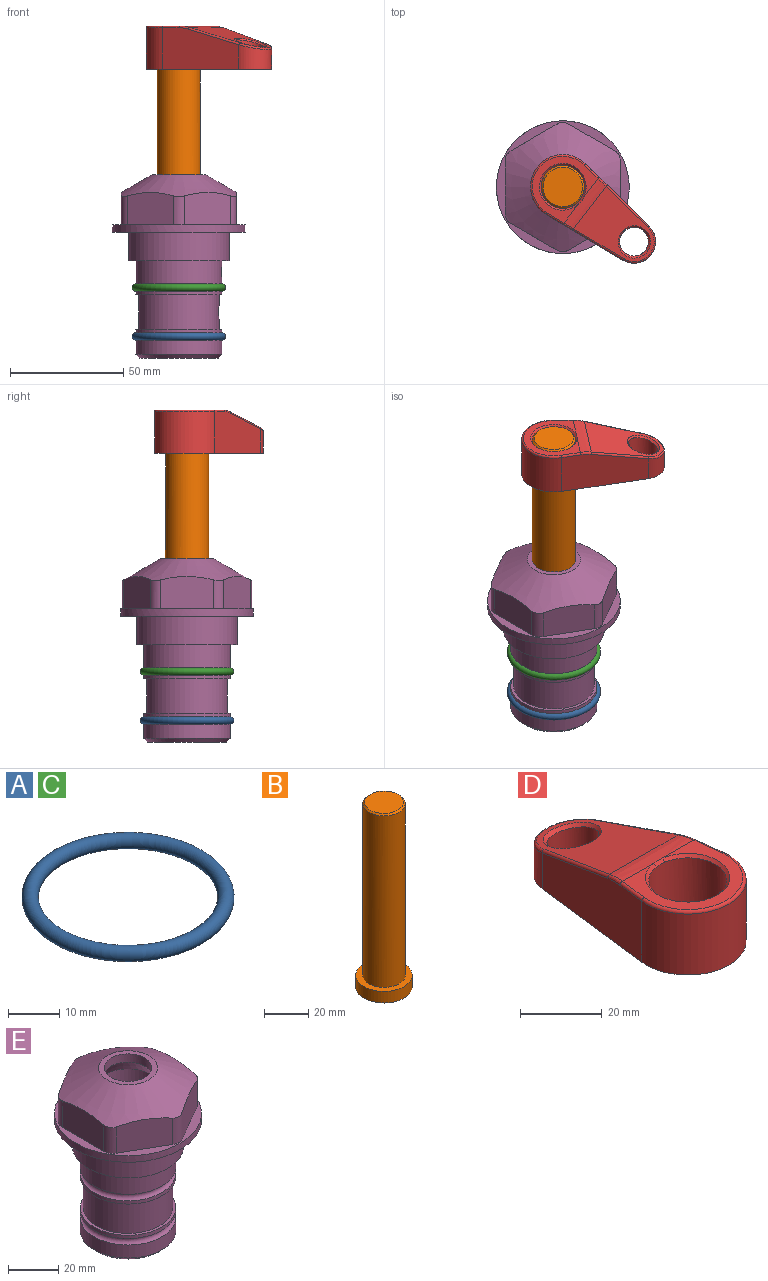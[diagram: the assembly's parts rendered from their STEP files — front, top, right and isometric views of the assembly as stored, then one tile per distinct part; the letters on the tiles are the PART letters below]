
ASSEMBLY  parts=5 mates=4
PART A: 1 faces, bbox 44.7x44.7x3.2 mm
  f0: torus R=19.05mm, axis (0,0,1), area 1193.9mm2
PART B: 6 faces, bbox 25.4x25.4x101.6 mm
  f0: plane 17.46x17.46mm, normal (0,0,1), area 239.5mm2, adj f5
  f1: plane 25.4x25.4mm, normal (0,0,-1), area 506.7mm2, adj f2
  f2: cylinder r=12.7mm len=25.4mm, axis (0,0,1), area 506.7mm2, adj f1,f3
  f3: plane 25.4x25.4mm, normal (0,0,1), area 221.7mm2, adj f2,f4
  f4: cylinder r=9.53mm len=94.46mm, axis (0,0,1), area 5653mm2, adj f3,f5
  f5: cone r=8.73mm half-angle=45deg, axis (0,0,-1), area 64.4mm2, adj f0,f4
PART C: same geometry as A
PART D: 31 faces, bbox 31.7x65.5x19.8 mm
  f0: plane 39.12x18.26mm, normal (0.99,0.12,0), area 612.2mm2, adj f1,f4,f7,f11,f13,f15
  f1: cylinder r=9.53mm len=18.91mm, axis (0,0,-1), area 296.1mm2, adj f0,f2,f7,f17
  f2: plane 39.12x18.26mm, normal (-0.99,0.12,0), area 612.2mm2, adj f1,f4,f7,f12,f14,f16
  f3: cylinder r=6.35mm len=12.7mm, axis (0,0,-1), area 362.4mm2, adj f7,f18
  f4: cylinder r=14.29mm len=28.58mm, axis (0,0,-1), area 882.2mm2, adj f0,f2,f7,f10
  f5: cylinder r=9.53mm len=19.05mm, axis (0,0,-1), area 1092.6mm2, adj f7,f19,f20
  f6: plane 26.99x23.69mm, normal (0,0,1), area 216.2mm2, adj f9,f10,f11,f12,f19
  f7: plane 63.5x28.58mm, normal (0,0,-1), area 661.8mm2, adj f0,f1,f2,f3,f4,f5,f22,f23
  f8: plane 33.52x23.6mm, normal (0,0.26,0.97), area 486mm2, adj f9,f15,f16,f17,f18
  f9: cylinder r=19.05mm len=24.72mm, axis (1,0,0), area 120.4mm2, adj f6,f8,f13,f14,f20
  f10: torus R=13.49mm, axis (0,0,1), area 59mm2, adj f4,f6,f11,f12
  f11: cylinder r=0.79mm len=8.67mm, axis (0.12,-0.99,0), area 10.8mm2, adj f0,f6,f10,f13
  f12: cylinder r=0.79mm len=8.67mm, axis (0.12,0.99,0), area 10.8mm2, adj f2,f6,f10,f14
  f13: bspline ~4.95x1.42mm, area 6.1mm2, adj f0,f9,f11,f15
  f14: bspline ~4.95x1.42mm, area 6.1mm2, adj f2,f9,f12,f16
  f15: cylinder r=0.79mm len=25.95mm, axis (0.12,-0.96,0.26), area 32.9mm2, adj f0,f8,f13,f17
  f16: cylinder r=0.79mm len=25.95mm, axis (0.12,0.96,-0.26), area 32.9mm2, adj f2,f8,f14,f17
  f17: bspline ~18.91x8.38mm, area 30mm2, adj f1,f8,f15,f16
  f18: bspline ~14.29x14.29mm, area 48.3mm2, adj f3,f8
  f19: cone r=9.53mm half-angle=45deg, axis (0,0,1), area 66.5mm2, adj f5,f6,f20
  f20: bspline ~3.22x0.96mm, area 3.5mm2, adj f5,f9,f19
  f21: plane 2.75x2.72mm, normal (0,0,-1), area 2.9mm2, adj f23,f25,f28
  f22: plane 23.05x15.88mm, normal (-0.99,-0.12,0), area 323.6mm2, adj f7,f25,f26,f27,f28,f29
  f23: plane 23.05x15.88mm, normal (0.99,-0.12,0), area 323.6mm2, adj f7,f21,f25,f27,f28,f30
  f24: cylinder r=9.53mm len=10.69mm, axis (0,0,-1), area 114.7mm2, adj f7,f27,f29,f30
  f25: cylinder r=12.7mm len=20.59mm, axis (0,0,-1), area 381.1mm2, adj f7,f21,f22,f23,f26,f28
  f26: plane 2.75x2.72mm, normal (0,0,-1), area 2.9mm2, adj f22,f25,f28
  f27: plane 19.72x18.37mm, normal (0,-0.26,-0.97), area 291.8mm2, adj f22,f23,f24,f28,f29,f30
  f28: cylinder r=15.88mm len=19.92mm, axis (1,0,0), area 54.8mm2, adj f21,f22,f23,f25,f26,f27
  f29: cylinder r=1.59mm len=11mm, axis (0,0,-1), area 34.7mm2, adj f7,f22,f24,f27
  f30: cylinder r=1.59mm len=11mm, axis (0,0,-1), area 34.7mm2, adj f7,f23,f24,f27
PART E: 36 faces, bbox 58.7x58.7x81 mm
  f0: cylinder r=17.78mm len=35.56mm, axis (0,0,1), area 1670.8mm2, adj f23,f24,f31
  f1: cylinder r=19.05mm len=38.1mm, axis (0,0,1), area 1191.9mm2, adj f26,f27,f30
  f2: plane 58.66x58.66mm, normal (0,0,-1), area 1150.6mm2, adj f3,f28
  f3: cylinder r=29.33mm len=58.66mm, axis (0,0,-1), area 585.1mm2, adj f2,f4
  f4: plane 58.66x58.66mm, normal (0,0,1), area 475.9mm2, adj f3,f5,f6,f7,f8,f9,f10,f11
  f5: plane 20.32x14.34mm, normal (-0.5,0.87,0), area 324.4mm2, adj f4,f15,f16,f17
  f6: plane 20.32x14.34mm, normal (0.5,0.87,0), area 324.4mm2, adj f4,f14,f15,f17
  f7: plane 23.48x14.34mm, normal (1,0,0), area 324.4mm2, adj f4,f13,f14,f17
  f8: plane 20.32x14.34mm, normal (0.5,-0.87,0), area 324.4mm2, adj f4,f12,f13,f17
  f9: plane 20.32x14.34mm, normal (-0.5,-0.87,0), area 324.4mm2, adj f4,f11,f12,f17
  f10: plane 23.48x14.34mm, normal (-1,0,0), area 324.4mm2, adj f4,f11,f16,f17
  f11: cylinder r=5.08mm len=12.85mm, axis (0,0,-1), area 67.2mm2, adj f4,f9,f10,f17
  f12: cylinder r=5.08mm len=12.85mm, axis (0,0,-1), area 67.2mm2, adj f4,f8,f9,f17
  f13: cylinder r=5.08mm len=12.85mm, axis (0,0,-1), area 67.2mm2, adj f4,f7,f8,f17
  f14: cylinder r=5.08mm len=12.85mm, axis (0,0,-1), area 67.2mm2, adj f4,f6,f7,f17
  f15: cylinder r=5.08mm len=12.85mm, axis (0,0,-1), area 67.2mm2, adj f4,f5,f6,f17
  f16: cylinder r=5.08mm len=12.85mm, axis (0,0,-1), area 67.2mm2, adj f4,f5,f10,f17
  f17: cone r=11.73mm half-angle=60deg, axis (0,0,-1), area 2071.8mm2, adj f5,f6,f7,f8,f9,f10,f11,f12
  f18: plane 23.46x23.46mm, normal (0,0,1), area 147.4mm2, adj f17,f35
  f19: plane 34.93x34.93mm, normal (0,0,-1), area 958mm2, adj f29
  f20: cylinder r=19.05mm len=38.1mm, axis (0,0,1), area 760.1mm2, adj f21,f29
  f21: torus R=19.05mm, axis (0,0,1), area 565.3mm2, adj f20,f22
  f22: cylinder r=19.05mm len=38.1mm, axis (0,0,1), area 190mm2, adj f21,f23
  f23: plane 38.1x38.1mm, normal (0,0,1), area 146.9mm2, adj f0,f22
  f24: plane 38.1x38.1mm, normal (0,0,-1), area 146.9mm2, adj f0,f25
  f25: cylinder r=19.05mm len=38.1mm, axis (0,0,1), area 190mm2, adj f24,f26
  f26: torus R=19.05mm, axis (0,0,1), area 565.3mm2, adj f1,f25
  f27: plane 44.45x44.45mm, normal (0,0,-1), area 411.7mm2, adj f1,f28
  f28: cylinder r=22.23mm len=44.45mm, axis (0,0,1), area 1773.5mm2, adj f2,f27
  f29: cone r=19.05mm half-angle=45deg, axis (0,0,1), area 257.5mm2, adj f19,f20
  f30: cylinder r=3.17mm len=6.75mm, axis (-1,0,0), area 128mm2, adj f1,f33
  f31: cylinder r=3.17mm len=6.35mm, axis (-1,0,0), area 102.5mm2, adj f0,f33
  f32: plane 25.4x25.4mm, normal (0,0,1), area 506.7mm2, adj f33
  f33: cylinder r=12.7mm len=66.42mm, axis (0,0,-1), area 5236.2mm2, adj f30,f31,f32,f34
  f34: cone r=9.53mm half-angle=30deg, axis (0,0,-1), area 443.4mm2, adj f33,f35
  f35: cylinder r=9.53mm len=19.05mm, axis (0,0,-1), area 240.9mm2, adj f18,f34
PLACE A t=(0,0,-21.59)mm
PLACE B rot(axis=(0,0,-1),127.6deg) t=(0,0,27.55)mm
PLACE C at identity
PLACE D rot(axis=(0,0,-1),127.6deg) t=(0,0,27.55)mm
PLACE E at identity fixed
MATE fastened D.f4 <-> B.f2  axis (0,0,1) through (0,0,91.05)mm
MATE cylindrical E.f0 <-> B.f2  axis (0,0,1) through (0,0,-50.55)mm
MATE fastened C.f0 <-> E.f0  axis (0,0,1) through (0,0,-24.51)mm
MATE fastened A.f0 <-> E.f0  axis (0,0,1) through (0,0,-46.1)mm
